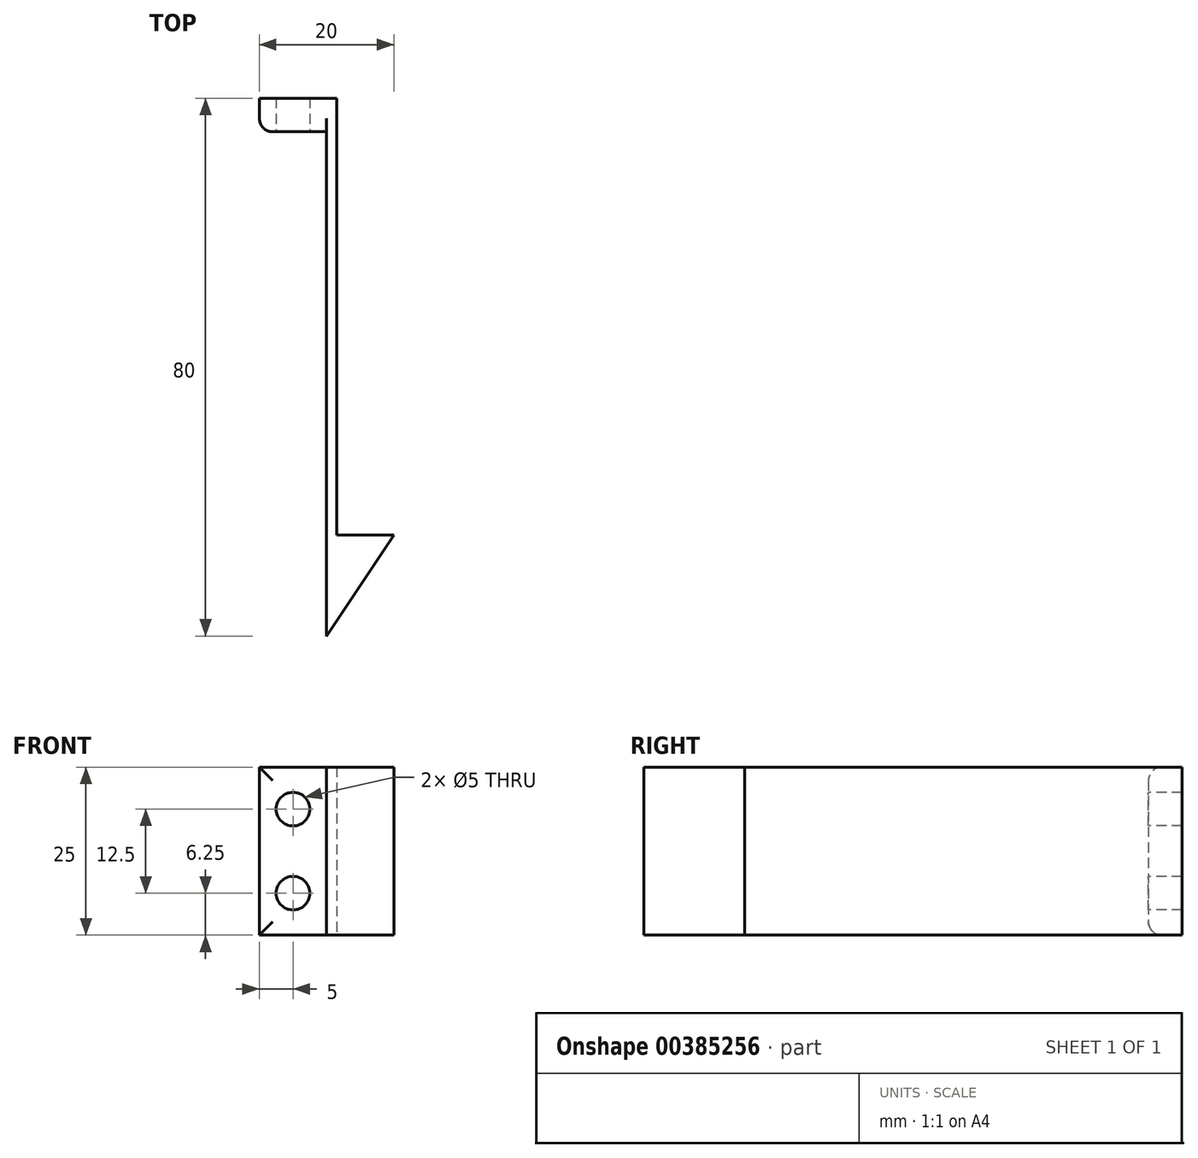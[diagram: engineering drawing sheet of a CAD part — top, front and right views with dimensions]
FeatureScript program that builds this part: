
annotation { "Feature Type Name" : "Feature", "Feature Type Description" : "" }
export const myFeature = defineFeature(function(context is Context, id is Id, definition is map)
    precondition{}
    {
        {
            var Q0;
            Q0=qCreatedBy(makeId("Top.planeOp"),FACE);
            var sketch = newSketch(context, id + "F0", { "sketchPlane" : qUnion([Q0])});
            skLineSegment(sketch, "E0", {"start": v(0, 0) * mm, "end": v(0, 65) * mm});
            skLineSegment(sketch, "E1", {"start": v(0, 65) * mm, "end": v(1.5, 65) * mm});
            skLineSegment(sketch, "E2", {"start": v(1.5, 65) * mm, "end": v(1.5, 0) * mm});
            skLineSegment(sketch, "E3", {"start": v(1.5, 0) * mm, "end": v(0, 0) * mm});
            skLineSegment(sketch, "E4.bottom", {"start": v(0, 0) * mm, "end": v(10, 0) * mm});
            skLineSegment(sketch, "E4.left", {"start": v(0, 0) * mm, "end": v(0, -15) * mm});
            skLineSegment(sketch, "E5", {"start": v(10, 0) * mm, "end": v(0, -15) * mm});
            skLineSegment(sketch, "E6.bottom", {"start": v(0, 65) * mm, "end": v(-10, 65) * mm});
            skLineSegment(sketch, "E6.top", {"start": v(0, 60) * mm, "end": v(-10, 60) * mm});
            skLineSegment(sketch, "E6.left", {"start": v(0, 65) * mm, "end": v(0, 60) * mm});
            skLineSegment(sketch, "E6.right", {"start": v(-10, 65) * mm, "end": v(-10, 60) * mm});
            skSolve(sketch);
        }
        {
            var Q0;
            Q0=makeQuery(id+"F0.imprint","IMPRINT",FACE,{"disambiguationData":[TD([[makeQuery(id+"F0.imprint","IMPRINT",EDGE,{"derivedFrom":sQuery(id+"F0.wireOp",EDGE,"E0")}),-1.0]])]});
            var Q1;
            {var subQ0=sQuery(id+"F0.wireOp",EDGE,"rakiuWBG-I9mv-oEl7-M0gU-fRtBCtiDM4VY");Q1=makeQuery(id+"F0.imprint","IMPRINT",FACE,{"disambiguationData":[TD([[makeQuery(id+"F0.imprint","IMPRINT",EDGE,{"derivedFrom":subQ0}),1.0]])]});}
            var Q2;
            Q2=makeQuery(id+"F0.imprint","IMPRINT",FACE,{"disambiguationData":[TD([[makeQuery(id+"F0.imprint","IMPRINT",EDGE,{"derivedFrom":sQuery(id+"F0.wireOp",EDGE,"E6.bottom")}),1.0]])]});
            var Q3;
            {var subQ0=sQuery(id+"F0.wireOp",EDGE,"E4.left");Q3=makeQuery(id+"F0.imprint","IMPRINT",FACE,{"disambiguationData":[TD([[makeQuery(id+"F0.imprint","IMPRINT",EDGE,{"derivedFrom":subQ0}),1.0]])]});}
            extrude(context, id + "F1", {"entities" : qUnion([Q0, Q1, Q2, Q3]), "depth" : 25 * mm});
        }
        {
            var Q0;
            Q0=makeQuery(id+"F1.opExtrude","SWEPT_FACE",FACE,{"disambiguationData":[OSD([sQuery(id+"F0.wireOp",EDGE,"E6.top")])]});
            var sketch = newSketch(context, id + "F2", { "sketchPlane" : qUnion([Q0])});
            skLineSegment(sketch, "E7", {"start": v(-5, 25) * mm, "end": v(-5, 0) * mm});
            skLineSegment(sketch, "E8", {"start": v(-5, 12.5) * mm, "end": v(-5, 0) * mm});
            skPoint(sketch, "E9", {"position": v(-5, 6.25) * mm});
            skLineSegment(sketch, "E10", {"start": v(-5, 12.5) * mm, "end": v(-5, 25) * mm});
            skPoint(sketch, "E11", {"position": v(-5, 18.75) * mm});
            skSolve(sketch);
        }
        {
            var Q0;
            Q0=sQuery(id+"F2.wireOp",VERTEX,"E11");
            var Q1;
            Q1=sQuery(id+"F2.wireOp",VERTEX,"E9");
            var Q2;
            Q2=makeQuery(id+"F1.opExtrude","SWEPT_BODY",BODY,{"disambiguationData":[OSD([sQuery(id+"F0.wireOp",EDGE,"E0"),sQuery(id+"F0.wireOp",EDGE,"E1"),sQuery(id+"F0.wireOp",EDGE,"E2"),sQuery(id+"F0.wireOp",EDGE,"E4.bottom"),sQuery(id+"F0.wireOp",EDGE,"E4.left"),sQuery(id+"F0.wireOp",EDGE,"E5"),sQuery(id+"F0.wireOp",EDGE,"E6.bottom"),sQuery(id+"F0.wireOp",EDGE,"E6.top"),sQuery(id+"F0.wireOp",EDGE,"E6.right")])]});
            hole(context, id + "F3", {"style" : HoleStyle.SIMPLE, "endStyle" : HoleEndStyle.THROUGH, "holeDiameter" : 5 * mm, "isTappedThrough" : true, "tappedDepth" : 12 * mm, "tapClearance" : 3, "locations" : qUnion([Q0, Q1]), "scope" : qUnion([Q2])});
        }
        {
            var Q0;
            Q0=makeQuery(id+"F1.opExtrude","SWEPT_EDGE",EDGE,{"disambiguationData":[OSD([sQuery(id+"F0.wireOp",EDGE,"E6.top"),sQuery(id+"F0.wireOp",EDGE,"E6.right")])]});
            var Q1;
            Q1=makeQuery(id+"F1.opExtrude","CAP_EDGE",EDGE,{"disambiguationData":[OSD([sQuery(id+"F0.wireOp",EDGE,"E6.top")])],"isStart":false});
            var Q2;
            Q2=makeQuery(id+"F1.opExtrude","CAP_EDGE",EDGE,{"disambiguationData":[OSD([sQuery(id+"F0.wireOp",EDGE,"E6.top")])],"isStart":true});
            fillet(context, id + "F4", {"entities" : qUnion([Q0, Q1, Q2]), "radius" : 2 * mm, "tangentPropagation" : true, "allowEdgeOverflow" : false});
        }
    });
